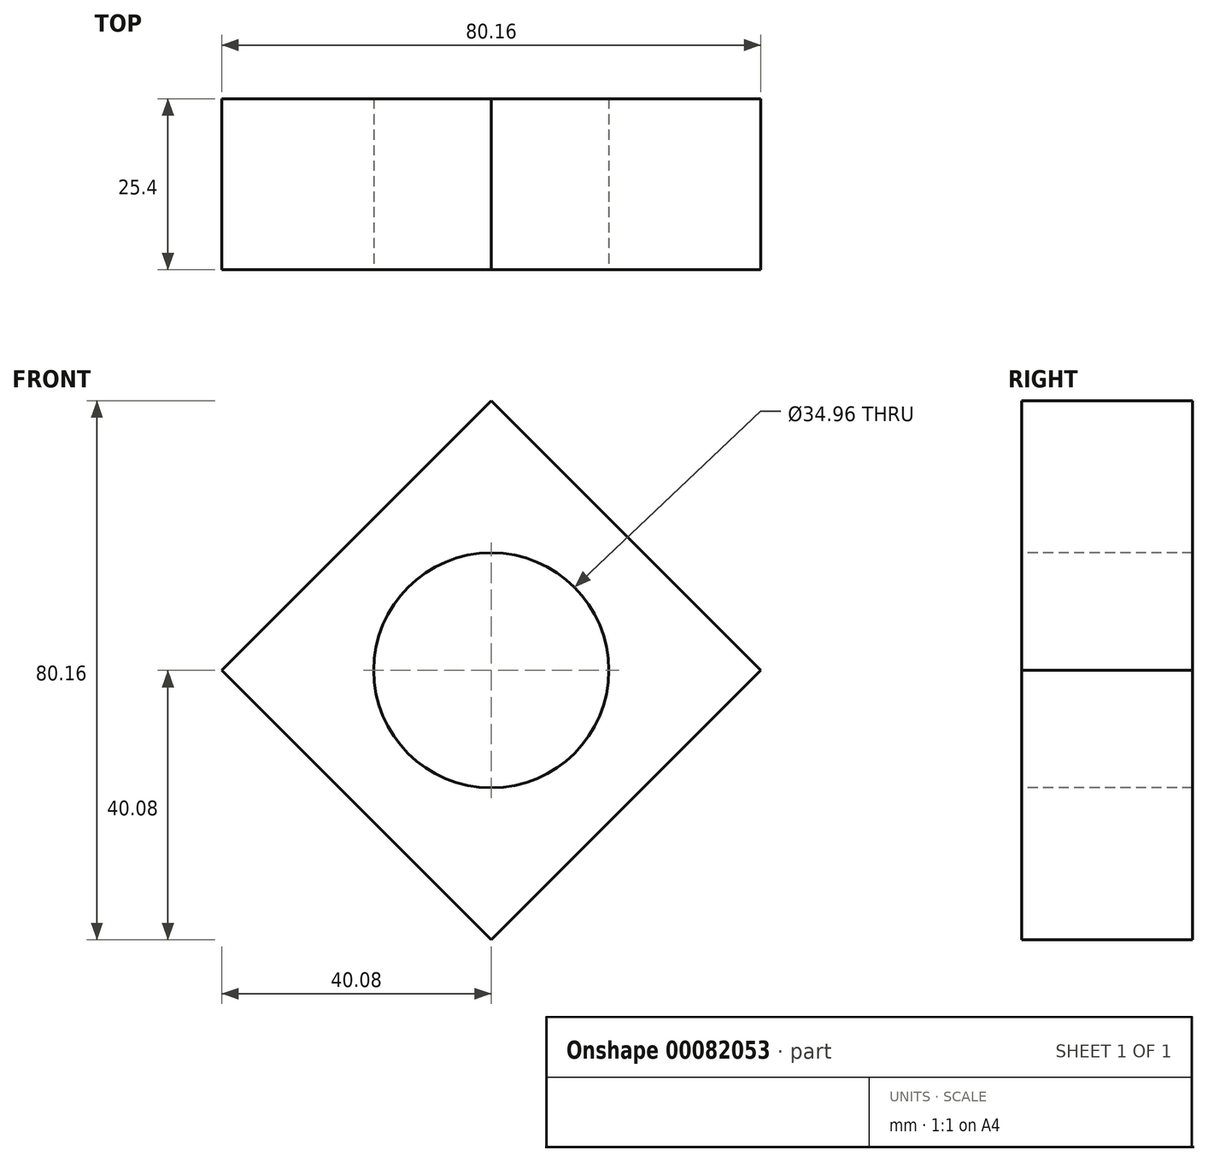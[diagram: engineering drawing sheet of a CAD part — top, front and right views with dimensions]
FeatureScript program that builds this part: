
annotation { "Feature Type Name" : "Feature", "Feature Type Description" : "" }
export const myFeature = defineFeature(function(context is Context, id is Id, definition is map)
    precondition{}
    {
        {
            var Q0;
            Q0=qCreatedBy(makeId("Front.planeOp"),FACE);
            var sketch = newSketch(context, id + "F0", { "sketchPlane" : qUnion([Q0])});
            skLineSegment(sketch, "E0", {"start": v(0, 0) * mm, "end": v(71.84, 71.84) * mm});
            skLineSegment(sketch, "E1", {"start": v(0, 0) * mm, "end": v(71.84, -71.84) * mm});
            skLineSegment(sketch, "E2", {"start": v(0, 0) * mm, "end": v(-71.84, -71.84) * mm});
            skLineSegment(sketch, "E3", {"start": v(0, 0) * mm, "end": v(-71.84, 71.84) * mm});
            skLineSegment(sketch, "E4", {"start": v(-71.84, 71.84) * mm, "end": v(-21.04, 71.84) * mm});
            skLineSegment(sketch, "E5", {"start": v(71.84, 71.84) * mm, "end": v(21.04, 71.84) * mm});
            skLineSegment(sketch, "E6", {"start": v(21.04, 71.84) * mm, "end": v(0, 40.08) * mm});
            skLineSegment(sketch, "E7", {"start": v(-21.04, 71.84) * mm, "end": v(0, 40.08) * mm});
            skLineSegment(sketch, "E8", {"start": v(-71.84, 71.84) * mm, "end": v(-71.84, 21.04) * mm});
            skLineSegment(sketch, "E9", {"start": v(-71.84, -71.84) * mm, "end": v(-71.84, -21.04) * mm});
            skLineSegment(sketch, "E10", {"start": v(-71.84, -21.04) * mm, "end": v(-40.08, 0) * mm});
            skLineSegment(sketch, "E11", {"start": v(-71.84, 21.04) * mm, "end": v(-40.08, 0) * mm});
            skLineSegment(sketch, "E12", {"start": v(-71.84, -71.84) * mm, "end": v(-21.04, -71.84) * mm});
            skLineSegment(sketch, "E13", {"start": v(71.84, -71.84) * mm, "end": v(21.04, -71.84) * mm});
            skLineSegment(sketch, "E14", {"start": v(21.04, -71.84) * mm, "end": v(0, -40.08) * mm});
            skLineSegment(sketch, "E15", {"start": v(-21.04, -71.84) * mm, "end": v(0, -40.08) * mm});
            skLineSegment(sketch, "E16", {"start": v(71.84, 71.84) * mm, "end": v(71.84, 21.04) * mm});
            skLineSegment(sketch, "E17", {"start": v(71.84, -71.84) * mm, "end": v(71.84, -21.04) * mm});
            skLineSegment(sketch, "E18", {"start": v(71.84, -21.04) * mm, "end": v(40.08, 0) * mm});
            skLineSegment(sketch, "E19", {"start": v(71.84, 21.04) * mm, "end": v(40.08, 0) * mm});
            skLineSegment(sketch, "E20", {"start": v(0, 40.08) * mm, "end": v(-40.08, 0) * mm});
            skLineSegment(sketch, "E21", {"start": v(-40.08, 0) * mm, "end": v(0, -40.08) * mm});
            skLineSegment(sketch, "E22", {"start": v(0, -40.08) * mm, "end": v(40.08, 0) * mm});
            skLineSegment(sketch, "E23", {"start": v(40.08, 0) * mm, "end": v(0, 40.08) * mm});
            skLineSegment(sketch, "E24", {"start": v(0, 40.08) * mm, "end": v(0, 0) * mm});
            skLineSegment(sketch, "E25", {"start": v(0, 0) * mm, "end": v(-40.08, 0) * mm});
            skLineSegment(sketch, "E26", {"start": v(0, 0) * mm, "end": v(0, -40.08) * mm});
            skLineSegment(sketch, "E27", {"start": v(0, 0) * mm, "end": v(40.08, 0) * mm});
            skLineSegment(sketch, "E28", {"start": v(0, 0) * mm, "end": v(20.04, 20.04) * mm});
            skLineSegment(sketch, "E29", {"start": v(0, 0) * mm, "end": v(-20.04, -20.04) * mm});
            skLineSegment(sketch, "E30", {"start": v(0, 0) * mm, "end": v(-20.04, 20.04) * mm});
            skLineSegment(sketch, "E31", {"start": v(0, 0) * mm, "end": v(20.04, -20.04) * mm});
            skSolve(sketch);
        }
        {
            var Q0;
            Q0=qCreatedBy(makeId("Front.planeOp"),FACE);
            cPlane(context, id + "F1", {"entities" : qUnion([Q0]), "cplaneType" : CPlaneType.OFFSET, "offset" : 12.7 * mm, "width" : 152.4 * mm, "height" : 152.4 * mm});
        }
        {
            var Q0;
            {var subQ0=sQuery(id+"F0.wireOp",EDGE,"E0");Q0=makeQuery(id+"F0.imprint","IMPRINT",FACE,{"disambiguationData":[TD([[makeQuery(id+"F0.imprint","IMPRINT",EDGE,{"derivedFrom":subQ0}),1.0]])]});}
            var Q1;
            {var subQ0=sQuery(id+"F0.wireOp",EDGE,"E0");Q1=makeQuery(id+"F0.imprint","IMPRINT",FACE,{"disambiguationData":[TD([[makeQuery(id+"F0.imprint","IMPRINT",EDGE,{"derivedFrom":subQ0}),-1.0]])]});}
            var Q2;
            {var subQ0=sQuery(id+"F0.wireOp",EDGE,"E1");Q2=makeQuery(id+"F0.imprint","IMPRINT",FACE,{"disambiguationData":[TD([[makeQuery(id+"F0.imprint","IMPRINT",EDGE,{"derivedFrom":subQ0}),-1.0]])]});}
            var Q3;
            {var subQ0=sQuery(id+"F0.wireOp",EDGE,"E1");Q3=makeQuery(id+"F0.imprint","IMPRINT",FACE,{"disambiguationData":[TD([[makeQuery(id+"F0.imprint","IMPRINT",EDGE,{"derivedFrom":subQ0}),1.0]])]});}
            var Q4;
            {var subQ0=sQuery(id+"F0.wireOp",EDGE,"E2");Q4=makeQuery(id+"F0.imprint","IMPRINT",FACE,{"disambiguationData":[TD([[makeQuery(id+"F0.imprint","IMPRINT",EDGE,{"derivedFrom":subQ0}),-1.0]])]});}
            var Q5;
            {var subQ0=sQuery(id+"F0.wireOp",EDGE,"E2");Q5=makeQuery(id+"F0.imprint","IMPRINT",FACE,{"disambiguationData":[TD([[makeQuery(id+"F0.imprint","IMPRINT",EDGE,{"derivedFrom":subQ0}),1.0]])]});}
            var Q6;
            {var subQ0=sQuery(id+"F0.wireOp",EDGE,"E3");Q6=makeQuery(id+"F0.imprint","IMPRINT",FACE,{"disambiguationData":[TD([[makeQuery(id+"F0.imprint","IMPRINT",EDGE,{"derivedFrom":subQ0}),-1.0]])]});}
            var Q7;
            {var subQ0=sQuery(id+"F0.wireOp",EDGE,"E3");Q7=makeQuery(id+"F0.imprint","IMPRINT",FACE,{"disambiguationData":[TD([[makeQuery(id+"F0.imprint","IMPRINT",EDGE,{"derivedFrom":subQ0}),1.0]])]});}
            var Q8;
            {var subQ2=sQuery(id+"F0.wireOp",EDGE,"E25");Q8=makeQuery(id+"F0.imprint","IMPRINT",FACE,{"disambiguationData":[TD([[makeQuery(id+"F0.imprint","IMPRINT",EDGE,{"derivedFrom":subQ2}),-1.0]])]});}
            var Q9;
            {var subQ2=sQuery(id+"F0.wireOp",EDGE,"E26");Q9=makeQuery(id+"F0.imprint","IMPRINT",FACE,{"disambiguationData":[TD([[makeQuery(id+"F0.imprint","IMPRINT",EDGE,{"derivedFrom":subQ2}),-1.0]])]});}
            var Q10;
            {var subQ2=sQuery(id+"F0.wireOp",EDGE,"E27");Q10=makeQuery(id+"F0.imprint","IMPRINT",FACE,{"disambiguationData":[TD([[makeQuery(id+"F0.imprint","IMPRINT",EDGE,{"derivedFrom":subQ2}),-1.0]])]});}
            var Q11;
            {var subQ2=sQuery(id+"F0.wireOp",EDGE,"E24");Q11=makeQuery(id+"F0.imprint","IMPRINT",FACE,{"disambiguationData":[TD([[makeQuery(id+"F0.imprint","IMPRINT",EDGE,{"derivedFrom":subQ2}),1.0]])]});}
            extrude(context, id + "F2", {"entities" : qUnion([Q0, Q1, Q2, Q3, Q4, Q5, Q6, Q7, Q8, Q9, Q10, Q11]), "depth" : 25.4 * mm});
        }
        {
            var Q0;
            Q0=qCreatedBy(id+"F1.planeOp",FACE);
            var sketch = newSketch(context, id + "F3", { "sketchPlane" : qUnion([Q0])});
            skCircle(sketch, "E32", {"center": v(0, 0) * mm, "radius": 17.48 * mm});
            skSolve(sketch);
        }
        {
            var Q0;
            Q0 = qSketchRegion(id + "F3", true);
            extrude(context, id + "F4", {"entities" : qUnion([Q0]), "operationType" : NewBodyOperationType.REMOVE, "oppositeDirection" : true, "depth" : 12.7 * mm, "hasSecondDirection" : true, "secondDirectionOppositeDirection" : false, "secondDirectionDepth" : 12.7 * mm});
        }
    });
